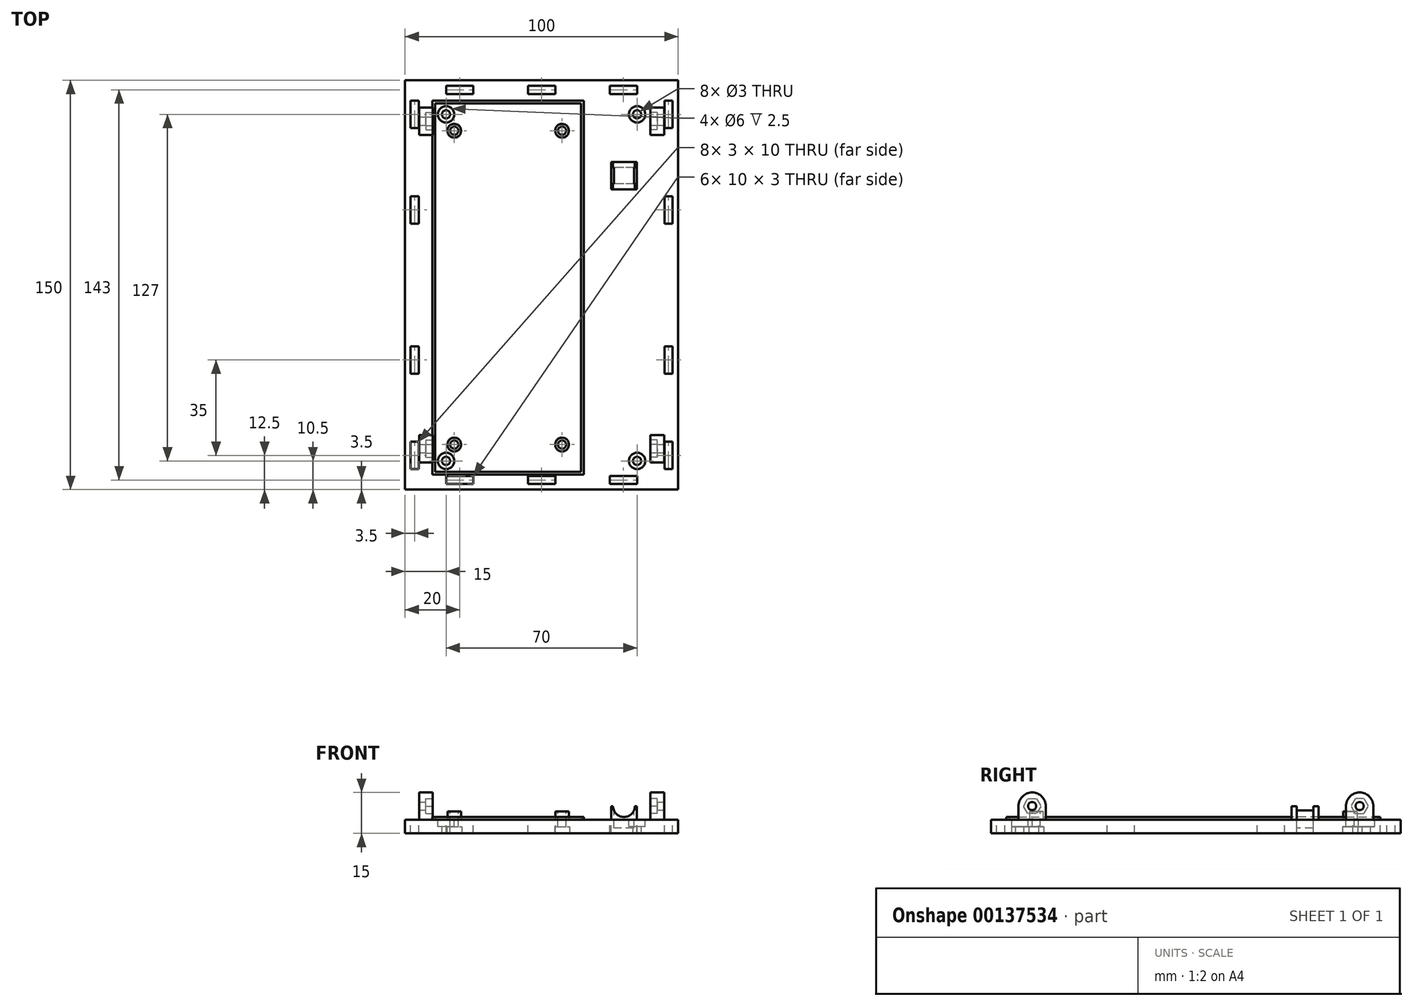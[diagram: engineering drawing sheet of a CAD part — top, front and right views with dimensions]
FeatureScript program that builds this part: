
annotation { "Feature Type Name" : "Feature", "Feature Type Description" : "" }
export const myFeature = defineFeature(function(context is Context, id is Id, definition is map)
    precondition{}
    {
        {
            var Q0;
            Q0=qCreatedBy(makeId("Top.planeOp"),FACE);
            var sketch = newSketch(context, id + "F0", { "sketchPlane" : qUnion([Q0])});
            skLineSegment(sketch, "E0.bottom", {"start": v(50, 75) * mm, "end": v(-50, 75) * mm});
            skLineSegment(sketch, "E0.top", {"start": v(50, -75) * mm, "end": v(-50, -75) * mm});
            skLineSegment(sketch, "E0.left", {"start": v(50, 75) * mm, "end": v(50, -75) * mm});
            skLineSegment(sketch, "E0.right", {"start": v(-50, 75) * mm, "end": v(-50, -75) * mm});
            skPoint(sketch, "E0.middle", {"position": v(0, 0) * mm});
            skSolve(sketch);
        }
        {
            var Q0;
            Q0=makeQuery(id+"F0.imprint","IMPRINT",FACE,{"disambiguationData":[TD([[makeQuery(id+"F0.imprint","IMPRINT",EDGE,{"derivedFrom":sQuery(id+"F0.wireOp",EDGE,"E0.bottom")}),1.0]])]});
            extrude(context, id + "F1", {"entities" : qUnion([Q0]), "depth" : 5 * mm});
        }
        {
            var Q0;
            Q0=makeQuery(id+"F1.opExtrude","CAP_FACE",FACE,{"disambiguationData":[OSD([sQuery(id+"F0.wireOp",EDGE,"E0.bottom"),sQuery(id+"F0.wireOp",EDGE,"E0.top"),sQuery(id+"F0.wireOp",EDGE,"E0.left"),sQuery(id+"F0.wireOp",EDGE,"E0.right")])],"isStart":false});
            var sketch = newSketch(context, id + "F2", { "sketchPlane" : qUnion([Q0])});
            skPoint(sketch, "E1.endSnap0", {"position": v(-50, 0) * mm});
            skCircle(sketch, "E2", {"center": v(-32, 56.5) * mm, "radius": 1.5 * mm});
            skCircle(sketch, "E3", {"center": v(7.5, 56.5) * mm, "radius": 1.5 * mm});
            skCircle(sketch, "E4", {"center": v(-32, -58.5) * mm, "radius": 1.5 * mm});
            skCircle(sketch, "E5", {"center": v(7.5, -58.5) * mm, "radius": 1.5 * mm});
            skSolve(sketch);
        }
        {
            var Q0;
            Q0 = qSketchRegion(id + "F2", true);
            var Q1;
            Q1 = qSketchRegion(id + "F4", true);
            extrude(context, id + "F3", {"entities" : qUnion([Q0, Q1]), "operationType" : NewBodyOperationType.REMOVE, "oppositeDirection" : true, "depth" : 25 * mm});
        }
        {
            var Q0;
            Q0=makeQuery(id+"F1.opExtrude","CAP_FACE",FACE,{"disambiguationData":[OSD([sQuery(id+"F0.wireOp",EDGE,"E0.bottom"),sQuery(id+"F0.wireOp",EDGE,"E0.top"),sQuery(id+"F0.wireOp",EDGE,"E0.left"),sQuery(id+"F0.wireOp",EDGE,"E0.right")])],"isStart":false});
            var sketch = newSketch(context, id + "F4", { "sketchPlane" : qUnion([Q0])});
            skCircle(sketch, "E6", {"center": v(-32, -58.5) * mm, "radius": 2.5 * mm});
            skCircle(sketch, "E7", {"center": v(7.5, -58.5) * mm, "radius": 2.5 * mm});
            skCircle(sketch, "E8", {"center": v(7.5, 56.5) * mm, "radius": 2.5 * mm});
            skCircle(sketch, "E9", {"center": v(-32, 56.5) * mm, "radius": 2.5 * mm});
            skCircle(sketch, "E10", {"center": v(-32, 56.5) * mm, "radius": 1.5 * mm});
            skCircle(sketch, "E11", {"center": v(7.5, 56.5) * mm, "radius": 1.5 * mm});
            skCircle(sketch, "E12", {"center": v(7.5, -58.5) * mm, "radius": 1.5 * mm});
            skCircle(sketch, "E13", {"center": v(-32, -58.5) * mm, "radius": 1.5 * mm});
            skSolve(sketch);
        }
        {
            var Q0;
            Q0 = qSketchRegion(id + "F4", true);
            extrude(context, id + "F5", {"entities" : qUnion([Q0]), "operationType" : NewBodyOperationType.ADD, "depth" : 3 * mm});
        }
        {
            var Q0;
            Q0=makeQuery(id+"F1.opExtrude","CAP_FACE",FACE,{"disambiguationData":[OSD([sQuery(id+"F0.wireOp",EDGE,"E0.bottom"),sQuery(id+"F0.wireOp",EDGE,"E0.top"),sQuery(id+"F0.wireOp",EDGE,"E0.left"),sQuery(id+"F0.wireOp",EDGE,"E0.right")])],"isStart":true});
            var sketch = newSketch(context, id + "F6", { "sketchPlane" : qUnion([Q0])});
            skCircle(sketch, "E14", {"center": v(-32, 58.5) * mm, "radius": 2.75 * mm});
            skCircle(sketch, "E15", {"center": v(7.5, 58.5) * mm, "radius": 2.75 * mm});
            skCircle(sketch, "E16", {"center": v(-32, -56.5) * mm, "radius": 2.75 * mm});
            skCircle(sketch, "E17", {"center": v(7.5, -56.5) * mm, "radius": 2.75 * mm});
            skSolve(sketch);
        }
        {
            var Q0;
            Q0 = qSketchRegion(id + "F6", true);
            extrude(context, id + "F7", {"entities" : qUnion([Q0]), "operationType" : NewBodyOperationType.REMOVE, "oppositeDirection" : true, "depth" : 2.5 * mm});
        }
        {
            var Q0;
            Q0=makeQuery(id+"F1.opExtrude","CAP_FACE",FACE,{"disambiguationData":[OSD([sQuery(id+"F0.wireOp",EDGE,"E0.bottom"),sQuery(id+"F0.wireOp",EDGE,"E0.top"),sQuery(id+"F0.wireOp",EDGE,"E0.left"),sQuery(id+"F0.wireOp",EDGE,"E0.right")])],"isStart":false});
            var sketch = newSketch(context, id + "F8", { "sketchPlane" : qUnion([Q0])});
            skLineSegment(sketch, "E18.bottom", {"start": v(-48, 67.5) * mm, "end": v(-45, 67.5) * mm});
            skLineSegment(sketch, "E18.top", {"start": v(-48, 57.5) * mm, "end": v(-45, 57.5) * mm});
            skLineSegment(sketch, "E18.left", {"start": v(-48, 67.5) * mm, "end": v(-48, 57.5) * mm});
            skLineSegment(sketch, "E18.right", {"start": v(-45, 67.5) * mm, "end": v(-45, 57.5) * mm});
            skLineSegment(sketch, "E19.bottom", {"start": v(-48, 32.5) * mm, "end": v(-45, 32.5) * mm});
            skLineSegment(sketch, "E19.top", {"start": v(-48, 22.5) * mm, "end": v(-45, 22.5) * mm});
            skLineSegment(sketch, "E19.left", {"start": v(-48, 32.5) * mm, "end": v(-48, 22.5) * mm});
            skLineSegment(sketch, "E19.right", {"start": v(-45, 32.5) * mm, "end": v(-45, 22.5) * mm});
            skLineSegment(sketch, "E20.bottom", {"start": v(-48, -22.5) * mm, "end": v(-45, -22.5) * mm});
            skLineSegment(sketch, "E20.top", {"start": v(-48, -32.5) * mm, "end": v(-45, -32.5) * mm});
            skLineSegment(sketch, "E20.left", {"start": v(-48, -22.5) * mm, "end": v(-48, -32.5) * mm});
            skLineSegment(sketch, "E20.right", {"start": v(-45, -22.5) * mm, "end": v(-45, -32.5) * mm});
            skLineSegment(sketch, "E21.bottom", {"start": v(-48, -57.5) * mm, "end": v(-45, -57.5) * mm});
            skLineSegment(sketch, "E21.top", {"start": v(-48, -67.5) * mm, "end": v(-45, -67.5) * mm});
            skLineSegment(sketch, "E21.left", {"start": v(-48, -57.5) * mm, "end": v(-48, -67.5) * mm});
            skLineSegment(sketch, "E21.right", {"start": v(-45, -57.5) * mm, "end": v(-45, -67.5) * mm});
            skLineSegment(sketch, "E22", {"start": v(0, 75) * mm, "end": v(0, -75) * mm});
            skLineSegment(sketch, "E23.MirrorCS", {"start": v(48, 67.5) * mm, "end": v(45, 67.5) * mm});
            skLineSegment(sketch, "E24.MirrorCS", {"start": v(48, -67.5) * mm, "end": v(45, -67.5) * mm});
            skLineSegment(sketch, "E25.MirrorCS", {"start": v(48, -57.5) * mm, "end": v(48, -67.5) * mm});
            skLineSegment(sketch, "E26.MirrorCS", {"start": v(48, -22.5) * mm, "end": v(48, -32.5) * mm});
            skLineSegment(sketch, "E27.MirrorCS", {"start": v(48, -32.5) * mm, "end": v(45, -32.5) * mm});
            skLineSegment(sketch, "E28.MirrorCS", {"start": v(48, -22.5) * mm, "end": v(45, -22.5) * mm});
            skLineSegment(sketch, "E29.MirrorCS", {"start": v(45, 32.5) * mm, "end": v(45, 22.5) * mm});
            skLineSegment(sketch, "E30.MirrorCS", {"start": v(45, -22.5) * mm, "end": v(45, -32.5) * mm});
            skLineSegment(sketch, "E31.MirrorCS", {"start": v(48, -57.5) * mm, "end": v(45, -57.5) * mm});
            skLineSegment(sketch, "E32.MirrorCS", {"start": v(45, -57.5) * mm, "end": v(45, -67.5) * mm});
            skLineSegment(sketch, "E33.MirrorCS", {"start": v(48, 32.5) * mm, "end": v(48, 22.5) * mm});
            skLineSegment(sketch, "E34.MirrorCS", {"start": v(48, 22.5) * mm, "end": v(45, 22.5) * mm});
            skLineSegment(sketch, "E35.MirrorCS", {"start": v(48, 32.5) * mm, "end": v(45, 32.5) * mm});
            skLineSegment(sketch, "E36.MirrorCS", {"start": v(45, 67.5) * mm, "end": v(45, 57.5) * mm});
            skLineSegment(sketch, "E37.MirrorCS", {"start": v(48, 57.5) * mm, "end": v(45, 57.5) * mm});
            skLineSegment(sketch, "E38.MirrorCS", {"start": v(48, 67.5) * mm, "end": v(48, 57.5) * mm});
            skLineSegment(sketch, "E39.bottom", {"start": v(-35, 73) * mm, "end": v(-25, 73) * mm});
            skLineSegment(sketch, "E39.top", {"start": v(-35, 70) * mm, "end": v(-25, 70) * mm});
            skLineSegment(sketch, "E39.left", {"start": v(-35, 73) * mm, "end": v(-35, 70) * mm});
            skLineSegment(sketch, "E39.right", {"start": v(-25, 73) * mm, "end": v(-25, 70) * mm});
            skLineSegment(sketch, "E40.bottom", {"start": v(-5, 73) * mm, "end": v(5, 73) * mm});
            skLineSegment(sketch, "E40.top", {"start": v(-5, 70) * mm, "end": v(5, 70) * mm});
            skLineSegment(sketch, "E40.left", {"start": v(-5, 73) * mm, "end": v(-5, 70) * mm});
            skLineSegment(sketch, "E40.right", {"start": v(5, 73) * mm, "end": v(5, 70) * mm});
            skLineSegment(sketch, "E41.bottom", {"start": v(25, 73) * mm, "end": v(35, 73) * mm});
            skLineSegment(sketch, "E41.top", {"start": v(25, 70) * mm, "end": v(35, 70) * mm});
            skLineSegment(sketch, "E41.left", {"start": v(25, 73) * mm, "end": v(25, 70) * mm});
            skLineSegment(sketch, "E41.right", {"start": v(35, 73) * mm, "end": v(35, 70) * mm});
            skLineSegment(sketch, "E42", {"start": v(-50, 0) * mm, "end": v(50, 0) * mm});
            skLineSegment(sketch, "E43.MirrorCS", {"start": v(25, -73) * mm, "end": v(25, -70) * mm});
            skLineSegment(sketch, "E44.MirrorCS", {"start": v(35, -73) * mm, "end": v(35, -70) * mm});
            skLineSegment(sketch, "E45.MirrorCS", {"start": v(5, -73) * mm, "end": v(5, -70) * mm});
            skLineSegment(sketch, "E46.MirrorCS", {"start": v(25, -70) * mm, "end": v(35, -70) * mm});
            skLineSegment(sketch, "E47.MirrorCS", {"start": v(25, -73) * mm, "end": v(35, -73) * mm});
            skLineSegment(sketch, "E48.MirrorCS", {"start": v(-5, -70) * mm, "end": v(5, -70) * mm});
            skLineSegment(sketch, "E49.MirrorCS", {"start": v(-5, -73) * mm, "end": v(5, -73) * mm});
            skLineSegment(sketch, "E50.MirrorCS", {"start": v(-5, -73) * mm, "end": v(-5, -70) * mm});
            skLineSegment(sketch, "E51.MirrorCS", {"start": v(-25, -73) * mm, "end": v(-25, -70) * mm});
            skLineSegment(sketch, "E52.MirrorCS", {"start": v(-35, -73) * mm, "end": v(-35, -70) * mm});
            skLineSegment(sketch, "E53.MirrorCS", {"start": v(-35, -73) * mm, "end": v(-25, -73) * mm});
            skLineSegment(sketch, "E54.MirrorCS", {"start": v(-35, -70) * mm, "end": v(-25, -70) * mm});
            skSolve(sketch);
        }
        {
            var Q0;
            Q0 = qSketchRegion(id + "F8", true);
            extrude(context, id + "F9", {"entities" : qUnion([Q0]), "operationType" : NewBodyOperationType.REMOVE, "oppositeDirection" : true, "depth" : 25 * mm});
        }
        {
            var Q0;
            Q0=makeQuery(id+"F1.opExtrude","CAP_FACE",FACE,{"disambiguationData":[OSD([sQuery(id+"F0.wireOp",EDGE,"E0.bottom"),sQuery(id+"F0.wireOp",EDGE,"E0.top"),sQuery(id+"F0.wireOp",EDGE,"E0.left"),sQuery(id+"F0.wireOp",EDGE,"E0.right")])],"isStart":false});
            var sketch = newSketch(context, id + "F10", { "sketchPlane" : qUnion([Q0])});
            skLineSegment(sketch, "E55", {"start": v(-39, 66.5) * mm, "end": v(14.5, 66.5) * mm});
            skLineSegment(sketch, "E56", {"start": v(14.5, 66.5) * mm, "end": v(14.5, -68.5) * mm});
            skLineSegment(sketch, "E57", {"start": v(14.5, -68.5) * mm, "end": v(-39, -68.5) * mm});
            skLineSegment(sketch, "E58", {"start": v(-39, -68.5) * mm, "end": v(-39, 66.5) * mm});
            skLineSegment(sketch, "E59.bottom", {"start": v(-40, 67.5) * mm, "end": v(15.5, 67.5) * mm});
            skLineSegment(sketch, "E59.top", {"start": v(-40, -69.5) * mm, "end": v(15.5, -69.5) * mm});
            skLineSegment(sketch, "E59.left", {"start": v(-40, 67.5) * mm, "end": v(-40, -69.5) * mm});
            skLineSegment(sketch, "E59.right", {"start": v(15.5, 67.5) * mm, "end": v(15.5, -69.5) * mm});
            skSolve(sketch);
        }
        {
            var Q0;
            Q0 = qSketchRegion(id + "F10", true);
            extrude(context, id + "F11", {"entities" : qUnion([Q0]), "operationType" : NewBodyOperationType.ADD, "depth" : 1 * mm});
        }
        {
            var Q0;
            {var subQ0=sQuery(id+"F0.wireOp",EDGE,"E0.left");var subQ1=sQuery(id+"F0.wireOp",EDGE,"E0.bottom");var subQ2=sQuery(id+"F0.wireOp",EDGE,"E0.top");var subQ3=sQuery(id+"F0.wireOp",EDGE,"E0.right");Q0=makeQuery(id+"F11.boolean.opBoolean","SPLIT",FACE,{"disambiguationData":[TD([makeQuery(id+"F1.opExtrude","SWEPT_FACE",FACE,{"disambiguationData":[OSD([subQ1])]})])],"derivedFrom":makeQuery(id+"F1.opExtrude","CAP_FACE",FACE,{"disambiguationData":[OSD([subQ1,subQ2,subQ0,subQ3])],"isStart":false})});}
            var sketch = newSketch(context, id + "F12", { "sketchPlane" : qUnion([Q0])});
            skLineSegment(sketch, "E60.bottom", {"start": v(25.5, 45) * mm, "end": v(34.85, 45) * mm});
            skLineSegment(sketch, "E60.top", {"start": v(25.5, 35) * mm, "end": v(34.85, 35) * mm});
            skLineSegment(sketch, "E60.left", {"start": v(25.5, 45) * mm, "end": v(25.5, 35) * mm});
            skLineSegment(sketch, "E60.right", {"start": v(34.85, 45) * mm, "end": v(34.85, 35) * mm});
            skLineSegment(sketch, "E61.bottom", {"start": v(25.5, 43) * mm, "end": v(26.5, 43) * mm});
            skLineSegment(sketch, "E61.top", {"start": v(25.5, 37) * mm, "end": v(26.5, 37) * mm});
            skLineSegment(sketch, "E61.left", {"start": v(25.5, 43) * mm, "end": v(25.5, 37) * mm});
            skLineSegment(sketch, "E61.right", {"start": v(26.5, 43) * mm, "end": v(26.5, 37) * mm});
            skLineSegment(sketch, "E62.bottom", {"start": v(34.85, 43) * mm, "end": v(33.85, 43) * mm});
            skLineSegment(sketch, "E62.top", {"start": v(34.85, 37) * mm, "end": v(33.85, 37) * mm});
            skLineSegment(sketch, "E62.left", {"start": v(34.85, 43) * mm, "end": v(34.85, 37) * mm});
            skLineSegment(sketch, "E62.right", {"start": v(33.85, 43) * mm, "end": v(33.85, 37) * mm});
            skSolve(sketch);
        }
        {
            var Q0;
            Q0 = qSketchRegion(id + "F12", true);
            extrude(context, id + "F13", {"entities" : qUnion([Q0]), "operationType" : NewBodyOperationType.ADD, "depth" : 5 * mm});
        }
        {
            var Q0;
            Q0=makeQuery(id+"F12.imprint","IMPRINT",FACE,{"disambiguationData":[TD([[makeQuery(id+"F12.imprint","IMPRINT",EDGE,{"derivedFrom":sQuery(id+"F12.wireOp",EDGE,"E62.bottom")}),1.0]])]});
            var Q1;
            Q1=makeQuery(id+"F12.imprint","IMPRINT",FACE,{"disambiguationData":[TD([[makeQuery(id+"F12.imprint","IMPRINT",EDGE,{"derivedFrom":sQuery(id+"F12.wireOp",EDGE,"E61.bottom")}),-1.0]])]});
            extrude(context, id + "F14", {"entities" : qUnion([Q0, Q1]), "operationType" : NewBodyOperationType.REMOVE, "endBound" : BoundingType.SYMMETRIC, "oppositeDirection" : true, "depth" : 25 * mm});
        }
        {
            var Q0;
            Q0=makeQuery(id+"F13.opExtrude","SWEPT_FACE",FACE,{"disambiguationData":[OSD([sQuery(id+"F12.wireOp",EDGE,"E60.top")])]});
            var sketch = newSketch(context, id + "F15", { "sketchPlane" : qUnion([Q0])});
            skCircle(sketch, "E63", {"center": v(30.18, 10) * mm, "radius": 4 * mm});
            skSolve(sketch);
        }
        {
            var Q0;
            Q0 = qSketchRegion(id + "F15", true);
            extrude(context, id + "F16", {"entities" : qUnion([Q0]), "operationType" : NewBodyOperationType.REMOVE, "oppositeDirection" : true, "depth" : 25 * mm});
        }
        {
            var Q0;
            Q0=makeQuery(id+"F1.opExtrude","CAP_FACE",FACE,{"disambiguationData":[OSD([sQuery(id+"F0.wireOp",EDGE,"E0.bottom"),sQuery(id+"F0.wireOp",EDGE,"E0.top"),sQuery(id+"F0.wireOp",EDGE,"E0.left"),sQuery(id+"F0.wireOp",EDGE,"E0.right")])],"isStart":true});
            var sketch = newSketch(context, id + "F17", { "sketchPlane" : qUnion([Q0])});
            skLineSegment(sketch, "E64.bottom", {"start": v(25.5, -37) * mm, "end": v(34.85, -37) * mm});
            skLineSegment(sketch, "E64.top", {"start": v(25.5, -43) * mm, "end": v(34.85, -43) * mm});
            skLineSegment(sketch, "E64.left", {"start": v(25.5, -37) * mm, "end": v(25.5, -43) * mm});
            skLineSegment(sketch, "E64.right", {"start": v(34.85, -37) * mm, "end": v(34.85, -43) * mm});
            skSolve(sketch);
        }
        {
            var Q0;
            Q0 = qSketchRegion(id + "F17", true);
            extrude(context, id + "F18", {"entities" : qUnion([Q0]), "operationType" : NewBodyOperationType.REMOVE, "oppositeDirection" : true, "depth" : 2 * mm});
        }
        {
            var Q0;
            {var subQ0=sQuery(id+"F0.wireOp",EDGE,"E0.left");var subQ1=sQuery(id+"F0.wireOp",EDGE,"E0.bottom");var subQ2=sQuery(id+"F0.wireOp",EDGE,"E0.top");var subQ3=sQuery(id+"F0.wireOp",EDGE,"E0.right");Q0=makeQuery(id+"F11.boolean.opBoolean","SPLIT",FACE,{"disambiguationData":[TD([makeQuery(id+"F1.opExtrude","SWEPT_FACE",FACE,{"disambiguationData":[OSD([subQ1])]})])],"derivedFrom":makeQuery(id+"F1.opExtrude","CAP_FACE",FACE,{"disambiguationData":[OSD([subQ1,subQ2,subQ0,subQ3])],"isStart":false})});}
            var sketch = newSketch(context, id + "F19", { "sketchPlane" : qUnion([Q0])});
            skLineSegment(sketch, "E65.bottom", {"start": v(39.9, 65) * mm, "end": v(44.9, 65) * mm});
            skLineSegment(sketch, "E65.top", {"start": v(39.9, 55) * mm, "end": v(44.9, 55) * mm});
            skLineSegment(sketch, "E65.left", {"start": v(39.9, 65) * mm, "end": v(39.9, 55) * mm});
            skLineSegment(sketch, "E65.right", {"start": v(44.9, 65) * mm, "end": v(44.9, 55) * mm});
            skLineSegment(sketch, "E66.bottom", {"start": v(-44.9, 65) * mm, "end": v(-39.9, 65) * mm});
            skLineSegment(sketch, "E66.top", {"start": v(-44.9, 55) * mm, "end": v(-39.9, 55) * mm});
            skLineSegment(sketch, "E66.left", {"start": v(-44.9, 65) * mm, "end": v(-44.9, 55) * mm});
            skLineSegment(sketch, "E66.right", {"start": v(-39.9, 65) * mm, "end": v(-39.9, 55) * mm});
            skLineSegment(sketch, "E67.bottom", {"start": v(-44.9, -55) * mm, "end": v(-39.9, -55) * mm});
            skLineSegment(sketch, "E67.top", {"start": v(-44.9, -65) * mm, "end": v(-39.9, -65) * mm});
            skLineSegment(sketch, "E67.left", {"start": v(-44.9, -55) * mm, "end": v(-44.9, -65) * mm});
            skLineSegment(sketch, "E67.right", {"start": v(-39.9, -55) * mm, "end": v(-39.9, -65) * mm});
            skLineSegment(sketch, "E68.bottom", {"start": v(39.9, -55) * mm, "end": v(44.9, -55) * mm});
            skLineSegment(sketch, "E68.top", {"start": v(39.9, -65) * mm, "end": v(44.9, -65) * mm});
            skLineSegment(sketch, "E68.left", {"start": v(39.9, -55) * mm, "end": v(39.9, -65) * mm});
            skLineSegment(sketch, "E68.right", {"start": v(44.9, -55) * mm, "end": v(44.9, -65) * mm});
            skSolve(sketch);
        }
        {
            var Q0;
            Q0 = qSketchRegion(id + "F19", true);
            extrude(context, id + "F20", {"entities" : qUnion([Q0]), "operationType" : NewBodyOperationType.ADD, "depth" : 12 * mm});
        }
        {
            var Q0;
            Q0=makeQuery(id+"F20.opExtrude","SWEPT_FACE",FACE,{"disambiguationData":[OSD([sQuery(id+"F19.wireOp",EDGE,"E68.right")])]});
            var sketch = newSketch(context, id + "F21", { "sketchPlane" : qUnion([Q0])});
            skCircle(sketch, "E69", {"center": v(-60, 10) * mm, "radius": 1.5 * mm});
            skCircle(sketch, "E70.MirrorC", {"center": v(60, 10) * mm, "radius": 1.5 * mm});
            skSolve(sketch);
        }
        {
            var Q0;
            Q0 = qSketchRegion(id + "F21", true);
            extrude(context, id + "F22", {"entities" : qUnion([Q0]), "operationType" : NewBodyOperationType.REMOVE, "oppositeDirection" : true, "depth" : 150 * mm});
        }
        {
            var Q0;
            Q0=makeQuery(id+"F20.opExtrude","SWEPT_FACE",FACE,{"disambiguationData":[OSD([sQuery(id+"F19.wireOp",EDGE,"E65.left")])]});
            var sketch = newSketch(context, id + "F23", { "sketchPlane" : qUnion([Q0])});
            skCircle(sketch, "E71.cCircle", {"center": v(-60, 10) * mm, "radius": 2.75 * mm, "construction": true});
            skLineSegment(sketch, "E71.0", {"start": v(-61.59, 12.75) * mm, "end": v(-58.41, 12.75) * mm});
            skLineSegment(sketch, "E71.1", {"start": v(-58.41, 12.75) * mm, "end": v(-56.82, 10) * mm});
            skLineSegment(sketch, "E71.2", {"start": v(-56.82, 10) * mm, "end": v(-58.41, 7.25) * mm});
            skLineSegment(sketch, "E71.3", {"start": v(-58.41, 7.25) * mm, "end": v(-61.59, 7.25) * mm});
            skLineSegment(sketch, "E71.4", {"start": v(-61.59, 7.25) * mm, "end": v(-63.18, 10) * mm});
            skLineSegment(sketch, "E71.5", {"start": v(-63.18, 10) * mm, "end": v(-61.59, 12.75) * mm});
            skPoint(sketch, "E71.0.midPoint", {"position": v(-60, 12.75) * mm});
            skLineSegment(sketch, "E72.MirrorCS", {"start": v(63.18, 10) * mm, "end": v(61.59, 12.75) * mm});
            skLineSegment(sketch, "E73.MirrorCS", {"start": v(61.59, 7.25) * mm, "end": v(63.18, 10) * mm});
            skLineSegment(sketch, "E74.MirrorCS", {"start": v(58.41, 7.25) * mm, "end": v(61.59, 7.25) * mm});
            skLineSegment(sketch, "E75.MirrorCS", {"start": v(56.82, 10) * mm, "end": v(58.41, 7.25) * mm});
            skLineSegment(sketch, "E76.MirrorCS", {"start": v(58.41, 12.75) * mm, "end": v(56.82, 10) * mm});
            skLineSegment(sketch, "E77.MirrorCS", {"start": v(61.59, 12.75) * mm, "end": v(58.41, 12.75) * mm});
            skPoint(sketch, "E78.MirrorP", {"position": v(60, 12.75) * mm});
            skCircle(sketch, "E79.MirrorC", {"center": v(60, 10) * mm, "radius": 2.75 * mm, "construction": true});
            skSolve(sketch);
        }
        {
            var Q0;
            Q0 = qSketchRegion(id + "F23", true);
            extrude(context, id + "F24", {"entities" : qUnion([Q0]), "operationType" : NewBodyOperationType.REMOVE, "oppositeDirection" : true, "depth" : 2.5 * mm});
        }
        {
            var Q0;
            Q0=makeQuery(id+"F20.opExtrude","SWEPT_FACE",FACE,{"disambiguationData":[OSD([sQuery(id+"F19.wireOp",EDGE,"E67.right")])]});
            var sketch = newSketch(context, id + "F25", { "sketchPlane" : qUnion([Q0])});
            skCircle(sketch, "E80.cCircle", {"center": v(-60, 10) * mm, "radius": 2.75 * mm, "construction": true});
            skLineSegment(sketch, "E80.0", {"start": v(-61.59, 12.75) * mm, "end": v(-58.41, 12.75) * mm});
            skLineSegment(sketch, "E80.1", {"start": v(-58.41, 12.75) * mm, "end": v(-56.82, 10) * mm});
            skLineSegment(sketch, "E80.2", {"start": v(-56.82, 10) * mm, "end": v(-58.41, 7.25) * mm});
            skLineSegment(sketch, "E80.3", {"start": v(-58.41, 7.25) * mm, "end": v(-61.59, 7.25) * mm});
            skLineSegment(sketch, "E80.4", {"start": v(-61.59, 7.25) * mm, "end": v(-63.18, 10) * mm});
            skLineSegment(sketch, "E80.5", {"start": v(-63.18, 10) * mm, "end": v(-61.59, 12.75) * mm});
            skPoint(sketch, "E80.0.midPoint", {"position": v(-60, 12.75) * mm});
            skLineSegment(sketch, "E81.MirrorCS", {"start": v(63.18, 10) * mm, "end": v(61.59, 12.75) * mm});
            skLineSegment(sketch, "E82.MirrorCS", {"start": v(61.59, 7.25) * mm, "end": v(63.18, 10) * mm});
            skLineSegment(sketch, "E83.MirrorCS", {"start": v(58.41, 7.25) * mm, "end": v(61.59, 7.25) * mm});
            skLineSegment(sketch, "E84.MirrorCS", {"start": v(56.82, 10) * mm, "end": v(58.41, 7.25) * mm});
            skLineSegment(sketch, "E85.MirrorCS", {"start": v(58.41, 12.75) * mm, "end": v(56.82, 10) * mm});
            skLineSegment(sketch, "E86.MirrorCS", {"start": v(61.59, 12.75) * mm, "end": v(58.41, 12.75) * mm});
            skCircle(sketch, "E87.MirrorC", {"center": v(60, 10) * mm, "radius": 2.75 * mm, "construction": true});
            skPoint(sketch, "E88.MirrorP", {"position": v(60, 12.75) * mm});
            skSolve(sketch);
        }
        {
            var Q0;
            Q0 = qSketchRegion(id + "F25", true);
            extrude(context, id + "F26", {"entities" : qUnion([Q0]), "operationType" : NewBodyOperationType.REMOVE, "oppositeDirection" : true, "depth" : 2.5 * mm});
        }
        {
            var Q0;
            Q0=makeQuery(id+"F20.opExtrude","SWEPT_FACE",FACE,{"disambiguationData":[OSD([sQuery(id+"F19.wireOp",EDGE,"E68.right")])]});
            var sketch = newSketch(context, id + "F27", { "sketchPlane" : qUnion([Q0])});
            skArc(sketch, "E89", {"start": v(-55, 10) * mm, "mid": v(-60, 15) * mm, "end": v(-65, 10) * mm});
            skLineSegment(sketch, "E90", {"start": v(-65, 10) * mm, "end": v(-65, 17) * mm});
            skLineSegment(sketch, "E91", {"start": v(-65, 17) * mm, "end": v(-55, 17) * mm});
            skLineSegment(sketch, "E92", {"start": v(-55, 17) * mm, "end": v(-55, 10) * mm});
            skLineSegment(sketch, "E93.MirrorCS", {"start": v(65, 10) * mm, "end": v(65, 17) * mm});
            skArc(sketch, "E94.MirrorCS", {"start": v(55, 10) * mm, "mid": v(60, 15) * mm, "end": v(65, 10) * mm});
            skLineSegment(sketch, "E95.MirrorCS", {"start": v(65, 17) * mm, "end": v(55, 17) * mm});
            skLineSegment(sketch, "E96.MirrorCS", {"start": v(55, 17) * mm, "end": v(55, 10) * mm});
            skSolve(sketch);
        }
        {
            var Q0;
            Q0 = qSketchRegion(id + "F27", true);
            extrude(context, id + "F28", {"entities" : qUnion([Q0]), "operationType" : NewBodyOperationType.REMOVE, "oppositeDirection" : true, "depth" : 150 * mm});
        }
        {
            var Q0;
            {var subQ0=sQuery(id+"F0.wireOp",EDGE,"E0.left");var subQ1=sQuery(id+"F0.wireOp",EDGE,"E0.bottom");var subQ2=sQuery(id+"F0.wireOp",EDGE,"E0.top");var subQ3=sQuery(id+"F0.wireOp",EDGE,"E0.right");Q0=makeQuery(id+"F11.boolean.opBoolean","SPLIT",FACE,{"disambiguationData":[TD([makeQuery(id+"F1.opExtrude","SWEPT_FACE",FACE,{"disambiguationData":[OSD([subQ1])]})])],"derivedFrom":makeQuery(id+"F1.opExtrude","CAP_FACE",FACE,{"disambiguationData":[OSD([subQ1,subQ2,subQ0,subQ3])],"isStart":false})});}
            var sketch = newSketch(context, id + "F29", { "sketchPlane" : qUnion([Q0])});
            skCircle(sketch, "E97", {"center": v(-35, 62.5) * mm, "radius": 1.5 * mm});
            skCircle(sketch, "E98", {"center": v(35, 62.5) * mm, "radius": 1.5 * mm});
            skCircle(sketch, "E99", {"center": v(-35, -64.5) * mm, "radius": 1.5 * mm});
            skCircle(sketch, "E100", {"center": v(35, -64.5) * mm, "radius": 1.5 * mm});
            skSolve(sketch);
        }
        {
            var Q0;
            Q0 = qSketchRegion(id + "F29", true);
            extrude(context, id + "F30", {"entities" : qUnion([Q0]), "operationType" : NewBodyOperationType.REMOVE, "oppositeDirection" : true, "depth" : 25 * mm});
        }
        {
            var Q0;
            {var subQ0=sQuery(id+"F0.wireOp",EDGE,"E0.left");var subQ1=sQuery(id+"F0.wireOp",EDGE,"E0.bottom");var subQ2=sQuery(id+"F0.wireOp",EDGE,"E0.top");var subQ3=sQuery(id+"F0.wireOp",EDGE,"E0.right");Q0=makeQuery(id+"F11.boolean.opBoolean","SPLIT",FACE,{"disambiguationData":[TD([makeQuery(id+"F1.opExtrude","SWEPT_FACE",FACE,{"disambiguationData":[OSD([subQ1])]})])],"derivedFrom":makeQuery(id+"F1.opExtrude","CAP_FACE",FACE,{"disambiguationData":[OSD([subQ1,subQ2,subQ0,subQ3])],"isStart":false})});}
            var sketch = newSketch(context, id + "F31", { "sketchPlane" : qUnion([Q0])});
            skCircle(sketch, "E101", {"center": v(35, -64.5) * mm, "radius": 3 * mm});
            skCircle(sketch, "E102", {"center": v(35, 62.5) * mm, "radius": 3 * mm});
            skCircle(sketch, "E103", {"center": v(-35, 62.5) * mm, "radius": 3 * mm});
            skCircle(sketch, "E104", {"center": v(-35, -64.5) * mm, "radius": 3 * mm});
            skSolve(sketch);
        }
        {
            var Q0;
            Q0 = qSketchRegion(id + "F31", true);
            extrude(context, id + "F32", {"entities" : qUnion([Q0]), "operationType" : NewBodyOperationType.REMOVE, "oppositeDirection" : true, "depth" : 2.5 * mm});
        }
    });
